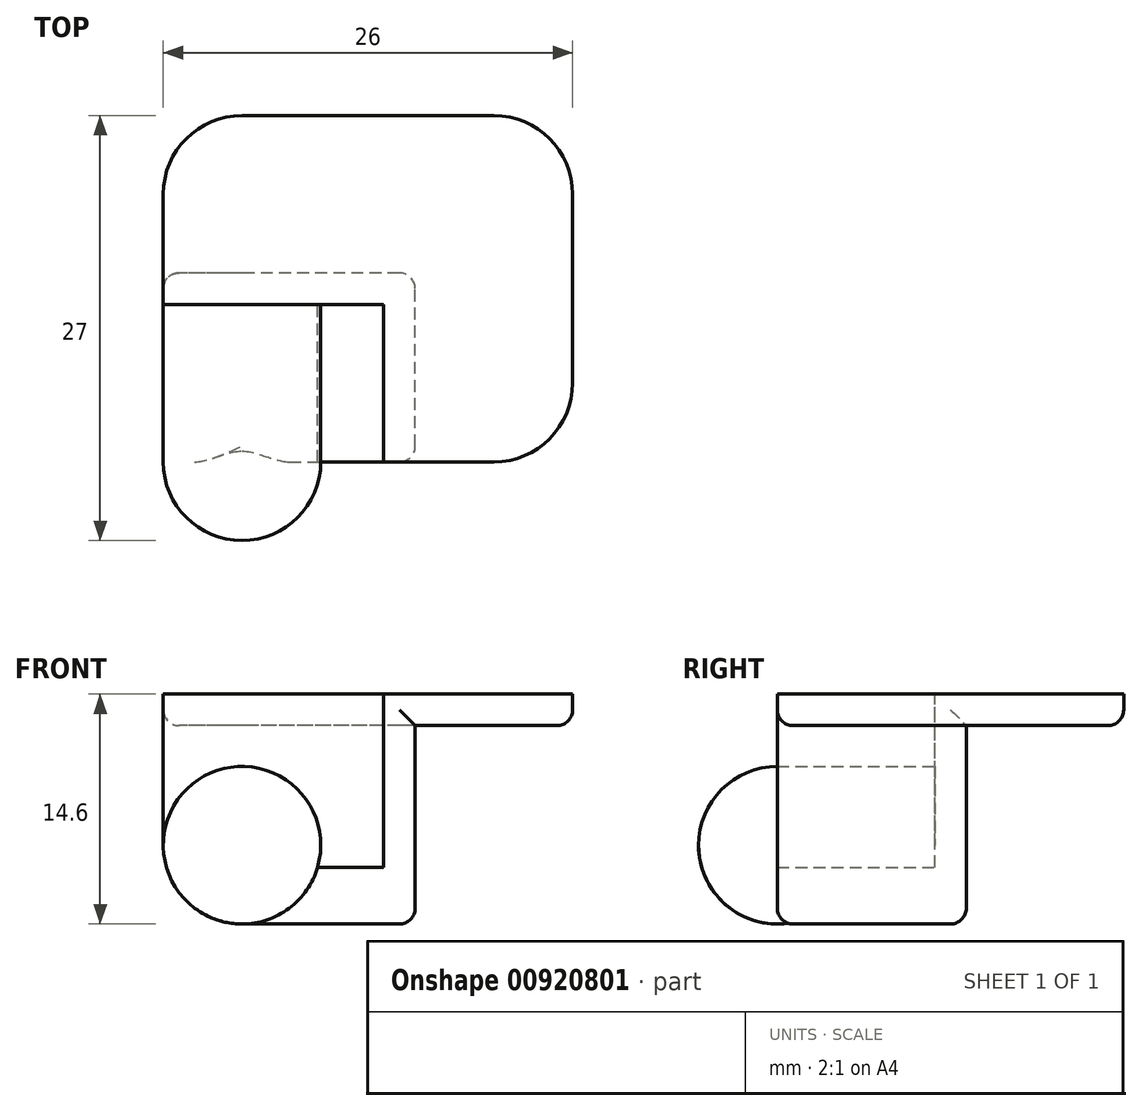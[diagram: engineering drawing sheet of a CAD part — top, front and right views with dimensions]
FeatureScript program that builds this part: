
annotation { "Feature Type Name" : "Feature", "Feature Type Description" : "" }
export const myFeature = defineFeature(function(context is Context, id is Id, definition is map)
    precondition{}
    {
        {
            var Q0;
            Q0=qCreatedBy(makeId("Front.planeOp"),FACE);
            var sketch = newSketch(context, id + "F0", { "sketchPlane" : qUnion([Q0])});
            skCircle(sketch, "E0", {"center": v(0, 0) * mm, "radius": 5 * mm});
            skLineSegment(sketch, "E1.bottom", {"start": v(0, -5) * mm, "end": v(9, -5) * mm});
            skLineSegment(sketch, "E1.top", {"start": v(0, -1.4) * mm, "end": v(9, -1.4) * mm});
            skLineSegment(sketch, "E1.left", {"start": v(0, -5) * mm, "end": v(0, -1.4) * mm});
            skLineSegment(sketch, "E1.right", {"start": v(9, -5) * mm, "end": v(9, -1.4) * mm});
            skLineSegment(sketch, "E2.bottom", {"start": v(9, -5) * mm, "end": v(11, -5) * mm});
            skLineSegment(sketch, "E2.top", {"start": v(9, 9.6) * mm, "end": v(11, 9.6) * mm});
            skLineSegment(sketch, "E2.left", {"start": v(9, -5) * mm, "end": v(9, 9.6) * mm});
            skLineSegment(sketch, "E2.right", {"start": v(11, -5) * mm, "end": v(11, 9.6) * mm});
            skSolve(sketch);
        }
        {
            var Q0;
            Q0 = qSketchRegion(id + "F0", true);
            extrude(context, id + "F1", {"entities" : qUnion([Q0]), "depth" : 10 * mm, "offsetDistance" : 25 * mm});
        }
        {
            var Q0;
            Q0=makeQuery(id+"F1.opExtrude","CAP_FACE",FACE,{"disambiguationData":[OSD([sQuery(id+"F0.wireOp",EDGE,"E0"),sQuery(id+"F0.wireOp",EDGE,"E1.bottom"),sQuery(id+"F0.wireOp",EDGE,"E1.top"),sQuery(id+"F0.wireOp",EDGE,"E2.bottom"),sQuery(id+"F0.wireOp",EDGE,"E2.top"),sQuery(id+"F0.wireOp",EDGE,"E2.left"),sQuery(id+"F0.wireOp",EDGE,"E2.right")])],"isStart":true});
            var sketch = newSketch(context, id + "F2", { "sketchPlane" : qUnion([Q0])});
            skLineSegment(sketch, "E3.bottom", {"start": v(-11, -5) * mm, "end": v(5, -5) * mm});
            skLineSegment(sketch, "E3.top", {"start": v(-11, 9.6) * mm, "end": v(5, 9.6) * mm});
            skLineSegment(sketch, "E3.left", {"start": v(-11, -5) * mm, "end": v(-11, 9.6) * mm});
            skLineSegment(sketch, "E3.right", {"start": v(5, -5) * mm, "end": v(5, 9.6) * mm});
            skSolve(sketch);
        }
        {
            var Q0;
            Q0 = qSketchRegion(id + "F2", true);
            extrude(context, id + "F3", {"entities" : qUnion([Q0]), "operationType" : NewBodyOperationType.ADD, "depth" : 2 * mm, "offsetDistance" : 25 * mm});
        }
        {
            var Q0;
            Q0=makeQuery(id+"F3.opExtrude","SWEPT_EDGE",EDGE,{"disambiguationData":[OSD([sQuery(id+"F2.wireOp",EDGE,"E3.bottom"),sQuery(id+"F2.wireOp",EDGE,"E3.right")])]});
            fillet(context, id + "F4", {"entities" : qUnion([Q0]), "radius" : 5 * mm, "tangentPropagation" : true, "allowEdgeOverflow" : false});
        }
        {
            var Q0;
            Q0=makeQuery(id+"F1.opExtrude","CAP_FACE",FACE,{"disambiguationData":[OSD([sQuery(id+"F0.wireOp",EDGE,"E0"),sQuery(id+"F0.wireOp",EDGE,"E1.bottom"),sQuery(id+"F0.wireOp",EDGE,"E1.top"),sQuery(id+"F0.wireOp",EDGE,"E2.bottom"),sQuery(id+"F0.wireOp",EDGE,"E2.top"),sQuery(id+"F0.wireOp",EDGE,"E2.left"),sQuery(id+"F0.wireOp",EDGE,"E2.right")])],"isStart":false});
            var sketch = newSketch(context, id + "F5", { "sketchPlane" : qUnion([Q0])});
            skCircle(sketch, "E4", {"center": v(0, 0) * mm, "radius": 5 * mm});
            skSolve(sketch);
        }
        {
            var Q0;
            {var subQ0=sQuery(id+"F5.wireOp",EDGE,"E4");var subQ2=makeQuery(id+"F5.imprint","INTERSECT",VERTEX,{"derivedFrom":[makeQuery(id+"F1.opExtrude","CAP_EDGE",EDGE,{"disambiguationData":[OSD([sQuery(id+"F0.wireOp",EDGE,"E1.top")])],"isStart":false}),subQ0]});Q0=makeQuery(id+"F5.imprint","IMPRINT",FACE,{"disambiguationData":[TD([[makeQuery(id+"F5.imprint","IMPRINT",EDGE,{"disambiguationData":[TD([[subQ2,1.0]])],"derivedFrom":subQ0}),1.0]])]});}
            extrude(context, id + "F6", {"entities" : qUnion([Q0]), "operationType" : NewBodyOperationType.ADD, "depth" : 5 * mm, "offsetDistance" : 25 * mm});
        }
        {
            var Q0;
            Q0=makeQuery(id+"F6.opExtrude","CAP_EDGE",EDGE,{"disambiguationData":[OSD([sQuery(id+"F5.wireOp",EDGE,"E4")])],"isStart":false});
            fillet(context, id + "F7", {"entities" : qUnion([Q0]), "radius" : 5 * mm, "tangentPropagation" : true, "allowEdgeOverflow" : false});
        }
        {
            var Q0;
            Q0=makeQuery(id+"F3.opExtrude","CAP_FACE",FACE,{"disambiguationData":[OSD([sQuery(id+"F2.wireOp",EDGE,"E3.bottom"),sQuery(id+"F2.wireOp",EDGE,"E3.top"),sQuery(id+"F2.wireOp",EDGE,"E3.left"),sQuery(id+"F2.wireOp",EDGE,"E3.right")])],"isStart":false});
            var sketch = newSketch(context, id + "F8", { "sketchPlane" : qUnion([Q0])});
            skLineSegment(sketch, "E5.bottom", {"start": v(-11, 9.6) * mm, "end": v(5, 9.6) * mm});
            skLineSegment(sketch, "E5.top", {"start": v(-11, 7.6) * mm, "end": v(5, 7.6) * mm});
            skLineSegment(sketch, "E5.left", {"start": v(-11, 9.6) * mm, "end": v(-11, 7.6) * mm});
            skLineSegment(sketch, "E5.right", {"start": v(5, 9.6) * mm, "end": v(5, 7.6) * mm});
            skSolve(sketch);
        }
        {
            var Q0;
            Q0 = qSketchRegion(id + "F8", true);
            extrude(context, id + "F9", {"entities" : qUnion([Q0]), "operationType" : NewBodyOperationType.ADD, "depth" : 10 * mm, "offsetDistance" : 25 * mm});
        }
        {
            var Q0;
            Q0=makeQuery(id+"F9.boolean.opBoolean","MERGE",FACE,{"derivedFrom":[makeQuery(id+"F3.boolean.opBoolean","MERGE",FACE,{"derivedFrom":[makeQuery(id+"F1.opExtrude","SWEPT_FACE",FACE,{"disambiguationData":[OSD([sQuery(id+"F0.wireOp",EDGE,"E2.right")])]}),makeQuery(id+"F3.opExtrude","SWEPT_FACE",FACE,{"disambiguationData":[OSD([sQuery(id+"F2.wireOp",EDGE,"E3.left")])]})]}),makeQuery(id+"F9.opExtrude","SWEPT_FACE",FACE,{"disambiguationData":[OSD([sQuery(id+"F8.wireOp",EDGE,"E5.left")])]})]});
            var sketch = newSketch(context, id + "F10", { "sketchPlane" : qUnion([Q0])});
            skLineSegment(sketch, "E6.bottom", {"start": v(-10, 9.6) * mm, "end": v(12, 9.6) * mm});
            skLineSegment(sketch, "E6.top", {"start": v(-10, 7.6) * mm, "end": v(12, 7.6) * mm});
            skLineSegment(sketch, "E6.left", {"start": v(-10, 9.6) * mm, "end": v(-10, 7.6) * mm});
            skLineSegment(sketch, "E6.right", {"start": v(12, 9.6) * mm, "end": v(12, 7.6) * mm});
            skSolve(sketch);
        }
        {
            var Q0;
            Q0 = qSketchRegion(id + "F10", true);
            extrude(context, id + "F11", {"entities" : qUnion([Q0]), "operationType" : NewBodyOperationType.ADD, "depth" : 10 * mm, "offsetDistance" : 25 * mm});
        }
        {
            var Q0;
            Q0=makeQuery(id+"F11.opExtrude","CAP_EDGE",EDGE,{"disambiguationData":[OSD([sQuery(id+"F10.wireOp",EDGE,"E6.left")])],"isStart":false});
            var Q1;
            Q1=makeQuery(id+"F11.opExtrude","CAP_EDGE",EDGE,{"disambiguationData":[OSD([sQuery(id+"F10.wireOp",EDGE,"E6.right")])],"isStart":false});
            var Q2;
            Q2=makeQuery(id+"F9.opExtrude","CAP_EDGE",EDGE,{"disambiguationData":[OSD([sQuery(id+"F8.wireOp",EDGE,"E5.right")])],"isStart":false});
            fillet(context, id + "F12", {"entities" : qUnion([Q0, Q1, Q2]), "radius" : 5 * mm, "tangentPropagation" : true, "allowEdgeOverflow" : false});
        }
        {
            var Q0;
            Q0=makeQuery(id+"F1.opExtrude","CAP_EDGE",EDGE,{"disambiguationData":[OSD([sQuery(id+"F0.wireOp",EDGE,"E1.bottom"),sQuery(id+"F0.wireOp",EDGE,"E2.bottom")])],"isStart":false});
            var Q1;
            Q1=makeQuery(id+"F1.opExtrude","CAP_EDGE",EDGE,{"disambiguationData":[OSD([sQuery(id+"F0.wireOp",EDGE,"E2.right")])],"isStart":false});
            var Q2;
            Q2=makeQuery(id+"F3.boolean.opBoolean","MERGE",EDGE,{"derivedFrom":[makeQuery(id+"F1.opExtrude","SWEPT_EDGE",EDGE,{"disambiguationData":[OSD([sQuery(id+"F0.wireOp",EDGE,"E2.bottom"),sQuery(id+"F0.wireOp",EDGE,"E2.right")])]}),makeQuery(id+"F3.opExtrude","SWEPT_EDGE",EDGE,{"disambiguationData":[OSD([sQuery(id+"F2.wireOp",EDGE,"E3.bottom"),sQuery(id+"F2.wireOp",EDGE,"E3.left")])]})]});
            var Q3;
            Q3=makeQuery(id+"F3.opExtrude","CAP_EDGE",EDGE,{"disambiguationData":[OSD([sQuery(id+"F2.wireOp",EDGE,"E3.left")])],"isStart":false});
            var Q4;
            Q4=makeQuery(id+"F3.opExtrude","CAP_EDGE",EDGE,{"disambiguationData":[OSD([sQuery(id+"F2.wireOp",EDGE,"E3.bottom")])],"isStart":false});
            var Q5;
            {var subQ0=sQuery(id+"F2.wireOp",EDGE,"E3.right");var subQ1=sQuery(id+"F2.wireOp",EDGE,"E3.bottom");Q5=makeQuery(id+"F4.opFillet","BLEND_EDGE",EDGE,{"blendedFrom":[makeQuery(id+"F3.opExtrude","SWEPT_EDGE",EDGE,{"disambiguationData":[OSD([subQ1,subQ0])]}),makeQuery(id+"F3.opExtrude","CAP_FACE",FACE,{"disambiguationData":[OSD([subQ1,sQuery(id+"F2.wireOp",EDGE,"E3.top"),sQuery(id+"F2.wireOp",EDGE,"E3.left"),subQ0])],"isStart":false})],"blendedInto":[makeQuery(id+"F3.opExtrude","CAP_FACE",FACE,{"disambiguationData":[OSD([subQ1,sQuery(id+"F2.wireOp",EDGE,"E3.top"),sQuery(id+"F2.wireOp",EDGE,"E3.left"),subQ0])],"isStart":false})]});}
            var Q6;
            Q6=makeQuery(id+"F3.opExtrude","CAP_EDGE",EDGE,{"disambiguationData":[OSD([sQuery(id+"F2.wireOp",EDGE,"E3.right")])],"isStart":false});
            var Q7;
            Q7=makeQuery(id+"F11.opExtrude","SWEPT_EDGE",EDGE,{"disambiguationData":[OSD([sQuery(id+"F0.wireOp",EDGE,"E2.right"),sQuery(id+"F10.wireOp",EDGE,"E6.top"),sQuery(id+"F10.wireOp",EDGE,"E6.left")])]});
            fillet(context, id + "F13", {"entities" : qUnion([Q0, Q1, Q2, Q3, Q4, Q5, Q6, Q7]), "radius" : 1 * mm, "tangentPropagation" : true, "allowEdgeOverflow" : false});
        }
    });
